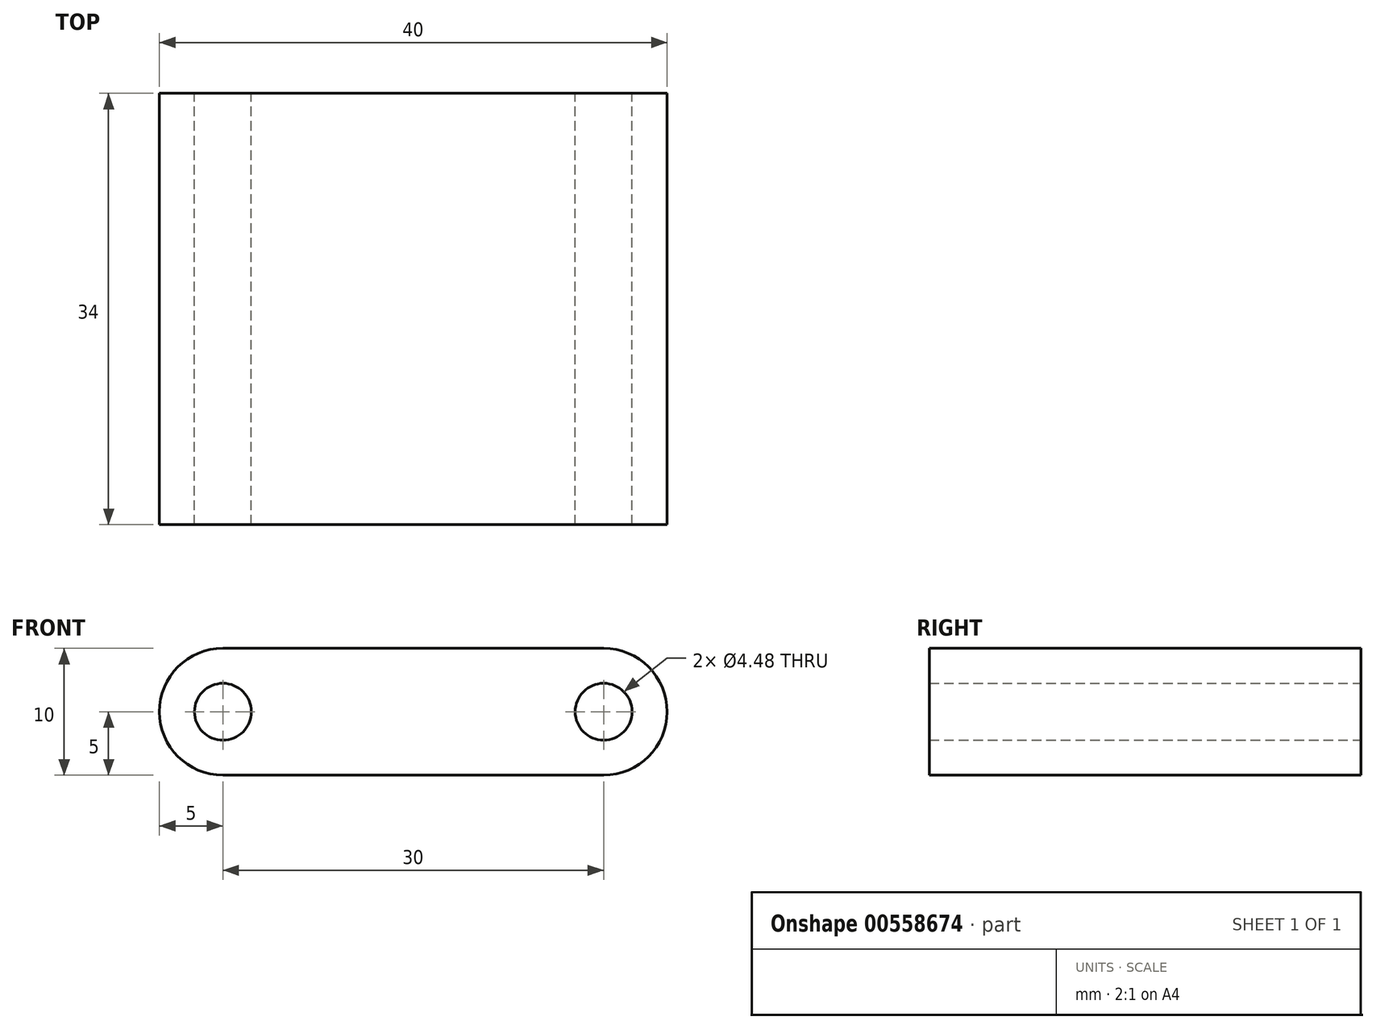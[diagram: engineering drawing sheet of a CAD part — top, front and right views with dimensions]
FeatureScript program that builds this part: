
annotation { "Feature Type Name" : "Feature", "Feature Type Description" : "" }
export const myFeature = defineFeature(function(context is Context, id is Id, definition is map)
    precondition{}
    {
        {
            var Q0;
            Q0=qCreatedBy(makeId("Front.planeOp"),FACE);
            var sketch = newSketch(context, id + "F0", { "sketchPlane" : qUnion([Q0])});
            skArc(sketch, "E0", {"start": v(-15, 5) * mm, "mid": v(-20, 0) * mm, "end": v(-15, -5) * mm});
            skArc(sketch, "E1", {"start": v(15, -5) * mm, "mid": v(20, 0) * mm, "end": v(15, 5) * mm});
            skLineSegment(sketch, "E2", {"start": v(-15, -5) * mm, "end": v(15, -5) * mm});
            skLineSegment(sketch, "E3", {"start": v(15, 5) * mm, "end": v(-15, 5) * mm});
            skLineSegment(sketch, "E4", {"start": v(-15, 0) * mm, "end": v(15, 0) * mm, "construction": true});
            skCircle(sketch, "E5", {"center": v(-15, 0) * mm, "radius": 2.24 * mm});
            skCircle(sketch, "E6", {"center": v(15, 0) * mm, "radius": 2.24 * mm});
            skSolve(sketch);
        }
        {
            var Q0;
            Q0=makeQuery(id+"F0.imprint","IMPRINT",FACE,{"disambiguationData":[TD([[makeQuery(id+"F0.imprint","IMPRINT",EDGE,{"derivedFrom":sQuery(id+"F0.wireOp",EDGE,"E0")}),1.0]])]});
            var Q1;
            Q1=qConstructionFilter(qBodyType(qCreatedBy(id+"F0",EDGE),BodyType.WIRE),ConstructionObject.NO);
            extrude(context, id + "F1", {"entities" : qUnion([Q0]), "surfaceEntities" : qUnion([Q1]), "endBound" : BoundingType.SYMMETRIC, "depth" : 34 * mm, "offsetDistance" : 25 * mm});
        }
    });
